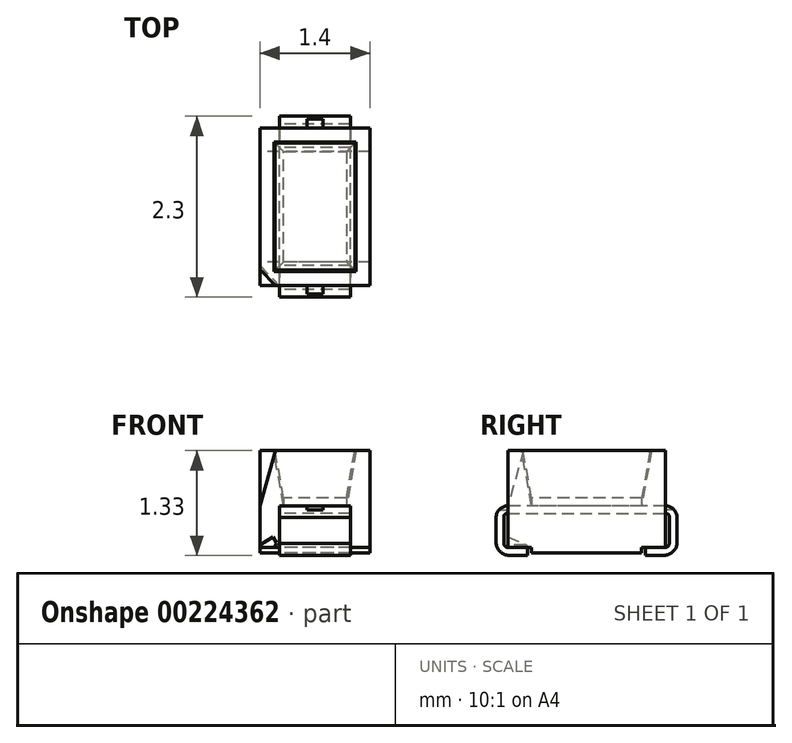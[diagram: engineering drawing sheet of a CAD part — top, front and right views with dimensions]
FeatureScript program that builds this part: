
annotation { "Feature Type Name" : "Feature", "Feature Type Description" : "" }
export const myFeature = defineFeature(function(context is Context, id is Id, definition is map)
    precondition{}
    {
        {
            var Q0;
            Q0=qCreatedBy(makeId("Top.planeOp"),FACE);
            var sketch = newSketch(context, id + "F0", { "sketchPlane" : qUnion([Q0])});
            skLineSegment(sketch, "E0.bottom", {"start": v(0.7, -1) * mm, "end": v(-0.7, -1) * mm});
            skLineSegment(sketch, "E0.top", {"start": v(0.7, 1) * mm, "end": v(-0.7, 1) * mm});
            skLineSegment(sketch, "E0.left", {"start": v(0.7, -1) * mm, "end": v(0.7, 1) * mm});
            skLineSegment(sketch, "E0.right", {"start": v(-0.7, -1) * mm, "end": v(-0.7, 1) * mm});
            skPoint(sketch, "E0.middle", {"position": v(0, 0) * mm});
            skLineSegment(sketch, "E1.bottom", {"start": v(0.4, -0.7) * mm, "end": v(-0.4, -0.7) * mm});
            skLineSegment(sketch, "E1.top", {"start": v(0.4, 0.7) * mm, "end": v(-0.4, 0.7) * mm});
            skLineSegment(sketch, "E1.left", {"start": v(0.4, -0.7) * mm, "end": v(0.4, 0.7) * mm});
            skLineSegment(sketch, "E1.right", {"start": v(-0.4, -0.7) * mm, "end": v(-0.4, 0.7) * mm});
            skLineSegment(sketch, "E2.bottom", {"start": v(0.15, -0.4) * mm, "end": v(-0.15, -0.4) * mm});
            skLineSegment(sketch, "E2.top", {"start": v(0.15, -0.1) * mm, "end": v(-0.15, -0.1) * mm});
            skLineSegment(sketch, "E2.left", {"start": v(0.15, -0.4) * mm, "end": v(0.15, -0.1) * mm});
            skLineSegment(sketch, "E2.right", {"start": v(-0.15, -0.4) * mm, "end": v(-0.15, -0.1) * mm});
            skPoint(sketch, "E2.middle", {"position": v(0, -0.25) * mm});
            skSolve(sketch);
        }
        {
            var Q0;
            Q0=makeQuery(id+"F0.imprint","IMPRINT",FACE,{"disambiguationData":[TD([[makeQuery(id+"F0.imprint","IMPRINT",EDGE,{"derivedFrom":sQuery(id+"F0.wireOp",EDGE,"E0.bottom")}),-1.0]])]});
            var Q1;
            {var subQ1=sQuery(id+"F0.wireOp",EDGE,"E0.top");Q1=makeQuery(id+"F0.imprint","IMPRINT",FACE,{"disambiguationData":[TD([[makeQuery(id+"F0.imprint","IMPRINT",EDGE,{"derivedFrom":subQ1}),1.0]])]});}
            extrude(context, id + "F1", {"entities" : qUnion([Q0, Q1]), "depth" : .7 * mm, "hasSecondDirection" : true, "secondDirectionOppositeDirection" : true, "secondDirectionDepth" : .6 * mm});
        }
        {
            var Q0;
            Q0=makeQuery(id+"F0.imprint","IMPRINT",FACE,{"disambiguationData":[TD([[makeQuery(id+"F0.imprint","IMPRINT",EDGE,{"derivedFrom":sQuery(id+"F0.wireOp",EDGE,"E1.bottom")}),-1.0]])]});
            var Q1;
            Q1=makeQuery(id+"F1.opExtrude","CAP_FACE",FACE,{"disambiguationData":[OSD([sQuery(id+"F0.wireOp",EDGE,"E0.bottom"),sQuery(id+"F0.wireOp",EDGE,"E0.top"),sQuery(id+"F0.wireOp",EDGE,"E0.left"),sQuery(id+"F0.wireOp",EDGE,"E0.right"),sQuery(id+"F0.wireOp",EDGE,"E1.bottom"),sQuery(id+"F0.wireOp",EDGE,"E1.top"),sQuery(id+"F0.wireOp",EDGE,"E1.left"),sQuery(id+"F0.wireOp",EDGE,"E1.right")])],"isStart":false});
            extrude(context, id + "F2", {"entities" : qUnion([Q0]), "operationType" : NewBodyOperationType.REMOVE, "endBound" : BoundingType.UP_TO_SURFACE, "endBoundEntityFace" : qUnion([Q1]), "depth" : 25 * mm, "hasDraft" : true, "draftAngle" : 10 * degree});
        }
        {
            var Q0;
            Q0=makeQuery(id+"F0.imprint","IMPRINT",FACE,{"disambiguationData":[TD([[makeQuery(id+"F0.imprint","IMPRINT",EDGE,{"derivedFrom":sQuery(id+"F0.wireOp",EDGE,"E2.bottom")}),-1.0]])]});
            extrude(context, id + "F3", {"entities" : qUnion([Q0]), "depth" : .1 * mm});
        }
        {
            var Q0;
            Q0=makeQuery(id+"F0.imprint","IMPRINT",FACE,{"disambiguationData":[TD([[makeQuery(id+"F0.imprint","IMPRINT",EDGE,{"derivedFrom":sQuery(id+"F0.wireOp",EDGE,"E1.bottom")}),-1.0]])]});
            var Q1;
            Q1=makeQuery(id+"F1.opExtrude","CAP_FACE",FACE,{"disambiguationData":[OSD([sQuery(id+"F0.wireOp",EDGE,"E0.bottom"),sQuery(id+"F0.wireOp",EDGE,"E0.top"),sQuery(id+"F0.wireOp",EDGE,"E0.left"),sQuery(id+"F0.wireOp",EDGE,"E0.right"),sQuery(id+"F0.wireOp",EDGE,"E1.bottom"),sQuery(id+"F0.wireOp",EDGE,"E1.top"),sQuery(id+"F0.wireOp",EDGE,"E1.left"),sQuery(id+"F0.wireOp",EDGE,"E1.right")])],"isStart":true});
            extrude(context, id + "F4", {"entities" : qUnion([Q0]), "operationType" : NewBodyOperationType.ADD, "endBound" : BoundingType.UP_TO_SURFACE, "oppositeDirection" : true, "endBoundEntityFace" : qUnion([Q1]), "depth" : 25 * mm});
        }
        {
            var Q0;
            Q0=makeQuery(id+"F0.imprint","IMPRINT",FACE,{"disambiguationData":[TD([[makeQuery(id+"F0.imprint","IMPRINT",EDGE,{"derivedFrom":sQuery(id+"F0.wireOp",EDGE,"E1.bottom")}),-1.0]])]});
            extrude(context, id + "F5", {"entities" : qUnion([Q0]), "depth" : .1 * mm});
        }
        {
            var Q0;
            Q0=makeQuery(id+"F0.imprint","IMPRINT",FACE,{"disambiguationData":[TD([[makeQuery(id+"F0.imprint","IMPRINT",EDGE,{"derivedFrom":sQuery(id+"F0.wireOp",EDGE,"E2.bottom")}),-1.0]])]});
            var Q1;
            {var subQ0=sQuery(id+"F0.wireOp",EDGE,"E1.right");var subQ1=sQuery(id+"F0.wireOp",EDGE,"E1.left");var subQ2=sQuery(id+"F0.wireOp",EDGE,"E1.top");var subQ3=sQuery(id+"F0.wireOp",EDGE,"E1.bottom");var subQ4=sQuery(id+"F0.wireOp",EDGE,"E0.right");var subQ5=sQuery(id+"F0.wireOp",EDGE,"E0.left");var subQ6=sQuery(id+"F0.wireOp",EDGE,"E0.top");var subQ7=sQuery(id+"F0.wireOp",EDGE,"E0.bottom");Q1=makeQuery(id+"F4.boolean.opBoolean","MERGE",FACE,{"derivedFrom":[makeQuery(id+"F1.opExtrude","CAP_FACE",FACE,{"disambiguationData":[OSD([subQ7,subQ6,subQ5,subQ4,subQ3,subQ2,subQ1,subQ0])],"isStart":true}),makeQuery(id+"F4.opExtrude","CAP_FACE",FACE,{"disambiguationData":[OSD([subQ7,subQ6,subQ5,subQ4,subQ3,subQ2,subQ1,subQ0])],"isStart":false})]});}
            extrude(context, id + "F6", {"entities" : qUnion([Q0]), "operationType" : NewBodyOperationType.ADD, "endBound" : BoundingType.UP_TO_SURFACE, "oppositeDirection" : true, "endBoundEntityFace" : qUnion([Q1]), "depth" : 25 * mm});
        }
        {
            var Q0;
            Q0=makeQuery(id+"F1.opExtrude","SWEPT_FACE",FACE,{"disambiguationData":[OSD([sQuery(id+"F0.wireOp",EDGE,"E0.right")])]});
            var sketch = newSketch(context, id + "F7", { "sketchPlane" : qUnion([Q0])});
            skLineSegment(sketch, "E3", {"start": v(-1, 0.7) * mm, "end": v(1, 0.7) * mm, "construction": true});
            skLineSegment(sketch, "E4", {"start": v(1, 0.7) * mm, "end": v(1, -0.6) * mm, "construction": true});
            skLineSegment(sketch, "E5", {"start": v(1, -0.6) * mm, "end": v(-1, -0.6) * mm, "construction": true});
            skLineSegment(sketch, "E6", {"start": v(-1, -0.6) * mm, "end": v(-1, 0.7) * mm, "construction": true});
            skLineSegment(sketch, "E7", {"start": v(-1.16, -0.53) * mm, "end": v(-0.7, -0.53) * mm});
            skLineSegment(sketch, "E8", {"start": v(-0.7, -0.53) * mm, "end": v(-0.7, -0.74) * mm});
            skLineSegment(sketch, "E9", {"start": v(-0.7, -0.74) * mm, "end": v(0.7, -0.74) * mm});
            skLineSegment(sketch, "E10", {"start": v(0.7, -0.74) * mm, "end": v(0.7, -0.53) * mm});
            skLineSegment(sketch, "E11", {"start": v(0.7, -0.53) * mm, "end": v(1.16, -0.53) * mm});
            skLineSegment(sketch, "E12", {"start": v(1.16, -0.53) * mm, "end": v(1.16, -0.97) * mm});
            skLineSegment(sketch, "E13", {"start": v(1.16, -0.97) * mm, "end": v(-1.16, -0.97) * mm});
            skLineSegment(sketch, "E14", {"start": v(-1.16, -0.97) * mm, "end": v(-1.16, -0.53) * mm});
            skSolve(sketch);
        }
        {
            var Q0;
            {var subQ0=sQuery(id+"F7.wireOp",EDGE,"E8");var subQ1=sQuery(id+"F7.wireOp",EDGE,"E7");var subQ2=makeQuery(id+"F7.imprint","INTERSECT",VERTEX,{"derivedFrom":[subQ1,subQ0]});Q0=makeQuery(id+"F7.imprint","IMPRINT",FACE,{"disambiguationData":[TD([[makeQuery(id+"F7.imprint","IMPRINT",EDGE,{"disambiguationData":[TD([[subQ2,-1.0]])],"derivedFrom":subQ0}),-1.0]])]});}
            var Q1;
            {var subQ0=sQuery(id+"F7.wireOp",EDGE,"E11");var subQ1=sQuery(id+"F7.wireOp",EDGE,"E10");var subQ2=makeQuery(id+"F7.imprint","INTERSECT",VERTEX,{"derivedFrom":[subQ1,subQ0]});Q1=makeQuery(id+"F7.imprint","IMPRINT",FACE,{"disambiguationData":[TD([[makeQuery(id+"F7.imprint","IMPRINT",EDGE,{"disambiguationData":[TD([[subQ2,1.0]])],"derivedFrom":subQ1}),-1.0]])]});}
            extrude(context, id + "F8", {"entities" : qUnion([Q0, Q1]), "operationType" : NewBodyOperationType.REMOVE, "endBound" : BoundingType.UP_TO_NEXT, "oppositeDirection" : true, "depth" : 25 * mm});
        }
        {
            var Q0;
            Q0=makeQuery(id+"F1.opExtrude","SWEPT_FACE",FACE,{"disambiguationData":[OSD([sQuery(id+"F0.wireOp",EDGE,"E0.right")])]});
            var sketch = newSketch(context, id + "F9", { "sketchPlane" : qUnion([Q0])});
            skLineSegment(sketch, "E15", {"start": v(-1, 0) * mm, "end": v(1, 0) * mm, "construction": true});
            skLineSegment(sketch, "E16", {"start": v(-1.15, -0.15) * mm, "end": v(-1.15, -0.48) * mm});
            skLineSegment(sketch, "E17", {"start": v(-1, -0.63) * mm, "end": v(-0.75, -0.63) * mm});
            skLineSegment(sketch, "E18", {"start": v(-1.15, 0) * mm, "end": v(1.15, 0) * mm});
            skLineSegment(sketch, "E19", {"start": v(1.15, -0.15) * mm, "end": v(1.15, -0.48) * mm});
            skLineSegment(sketch, "E20", {"start": v(1, -0.63) * mm, "end": v(0.75, -0.63) * mm});
            skLineSegment(sketch, "E21", {"start": v(0.75, -0.63) * mm, "end": v(0.75, -0.53) * mm});
            skLineSegment(sketch, "E22", {"start": v(0.75, -0.53) * mm, "end": v(1, -0.53) * mm});
            skLineSegment(sketch, "E23", {"start": v(1.05, -0.48) * mm, "end": v(1.05, -0.15) * mm});
            skLineSegment(sketch, "E24", {"start": v(1, -0.1) * mm, "end": v(-1, -0.1) * mm});
            skLineSegment(sketch, "E25", {"start": v(-1.05, -0.15) * mm, "end": v(-1.05, -0.48) * mm});
            skLineSegment(sketch, "E26", {"start": v(-1, -0.53) * mm, "end": v(-0.75, -0.53) * mm});
            skLineSegment(sketch, "E27", {"start": v(-0.75, -0.53) * mm, "end": v(-0.75, -0.63) * mm});
            skPoint(sketch, "E28.visualSharp", {"position": v(-1.05, -0.1) * mm});
            skArc(sketch, "E28.filletArc", {"start": v(-1, -0.1) * mm, "mid": v(-1.04, -0.11) * mm, "end": v(-1.05, -0.15) * mm});
            skPoint(sketch, "E29.newPointA", {"position": v(0, 0) * mm});
            skArc(sketch, "E29.filletArc", {"start": v(-1, 0) * mm, "mid": v(-1.1, -0.04) * mm, "end": v(-1.15, -0.15) * mm});
            skPoint(sketch, "E30.visualSharp", {"position": v(-1.15, -0.63) * mm});
            skArc(sketch, "E30.filletArc", {"start": v(-1.15, -0.48) * mm, "mid": v(-1.1, -0.58) * mm, "end": v(-1, -0.63) * mm});
            skPoint(sketch, "E31.visualSharp", {"position": v(-1.05, -0.53) * mm});
            skArc(sketch, "E31.filletArc", {"start": v(-1.05, -0.48) * mm, "mid": v(-1.04, -0.51) * mm, "end": v(-1, -0.53) * mm});
            skPoint(sketch, "E32.visualSharp", {"position": v(1.05, -0.53) * mm});
            skArc(sketch, "E32.filletArc", {"start": v(1, -0.53) * mm, "mid": v(1.04, -0.51) * mm, "end": v(1.05, -0.48) * mm});
            skPoint(sketch, "E33.visualSharp", {"position": v(1.05, -0.1) * mm});
            skArc(sketch, "E33.filletArc", {"start": v(1.05, -0.15) * mm, "mid": v(1.04, -0.11) * mm, "end": v(1, -0.1) * mm});
            skArc(sketch, "E34.filletArc", {"start": v(1.15, -0.15) * mm, "mid": v(1.1, -0.04) * mm, "end": v(1, 0) * mm});
            skPoint(sketch, "E35.visualSharp", {"position": v(1.15, -0.63) * mm});
            skArc(sketch, "E35.filletArc", {"start": v(1, -0.63) * mm, "mid": v(1.1, -0.58) * mm, "end": v(1.15, -0.48) * mm});
            skSolve(sketch);
        }
        {
            var Q0;
            Q0=qSketchRegion(id+"F9",true);
            var Q1;
            Q1=makeQuery(id+"F1.opExtrude","SWEPT_FACE",FACE,{"disambiguationData":[OSD([sQuery(id+"F0.wireOp",EDGE,"E0.left")])]});
            extrude(context, id + "F10", {"entities" : qUnion([Q0]), "oppositeDirection" : true, "endBoundEntityFace" : qUnion([Q1]), "depth" : 1.15 * mm, "hasSecondDirection" : true, "secondDirectionOppositeDirection" : true, "secondDirectionDepth" : .25 * mm});
        }
        {
            var Q0;
            Q0=makeQuery(id+"F5.opExtrude","CAP_FACE",FACE,{"disambiguationData":[OSD([sQuery(id+"F0.wireOp",EDGE,"E1.bottom"),sQuery(id+"F0.wireOp",EDGE,"E1.top"),sQuery(id+"F0.wireOp",EDGE,"E1.left"),sQuery(id+"F0.wireOp",EDGE,"E1.right"),sQuery(id+"F0.wireOp",EDGE,"E2.bottom"),sQuery(id+"F0.wireOp",EDGE,"E2.top"),sQuery(id+"F0.wireOp",EDGE,"E2.left"),sQuery(id+"F0.wireOp",EDGE,"E2.right")])],"isStart":false});
            var sketch = newSketch(context, id + "F11", { "sketchPlane" : qUnion([Q0])});
            skLineSegment(sketch, "E36.0.1", {"start": v(-0.45, 1) * mm, "end": v(0.45, 1) * mm});
            skLineSegment(sketch, "E37", {"start": v(0, 1) * mm, "end": v(0.1, 1) * mm});
            skLineSegment(sketch, "E38", {"start": v(0.1, 1) * mm, "end": v(0.1, 1.2) * mm});
            skLineSegment(sketch, "E39", {"start": v(0.1, 1.2) * mm, "end": v(-0.1, 1.2) * mm});
            skLineSegment(sketch, "E40", {"start": v(-0.1, 1.2) * mm, "end": v(-0.1, 1) * mm});
            skLineSegment(sketch, "E41", {"start": v(-0.1, 1) * mm, "end": v(0, 1) * mm});
            skPoint(sketch, "E42.startSnap0", {"position": v(-0.15, -0.25) * mm});
            skPoint(sketch, "E36.0.2.end.orphan", {"position": v(0.45, 1.15) * mm});
            skPoint(sketch, "E36.0.0.start.orphan", {"position": v(-0.45, 1.15) * mm});
            skLineSegment(sketch, "E43", {"start": v(-0.78, 0) * mm, "end": v(1.2, 0) * mm, "construction": true});
            skLineSegment(sketch, "E44.MirrorCS", {"start": v(-0.1, -1) * mm, "end": v(0, -1) * mm});
            skLineSegment(sketch, "E45.MirrorCS", {"start": v(-0.1, -1.2) * mm, "end": v(-0.1, -1) * mm});
            skLineSegment(sketch, "E46.MirrorCS", {"start": v(0, -1) * mm, "end": v(0.1, -1) * mm});
            skLineSegment(sketch, "E47.MirrorCS", {"start": v(0.1, -1.2) * mm, "end": v(-0.1, -1.2) * mm});
            skLineSegment(sketch, "E48.MirrorCS", {"start": v(0.1, -1) * mm, "end": v(0.1, -1.2) * mm});
            skSolve(sketch);
        }
        {
            var Q0;
            Q0=qSketchRegion(id+"F11",true);
            extrude(context, id + "F12", {"entities" : qUnion([Q0]), "operationType" : NewBodyOperationType.REMOVE, "oppositeDirection" : true, "depth" : .15 * mm});
        }
        {
            var Q0;
            Q0=makeQuery(id+"F1.opExtrude","SWEPT_FACE",FACE,{"disambiguationData":[OSD([sQuery(id+"F0.wireOp",EDGE,"E0.bottom")])]});
            var sketch = newSketch(context, id + "F13", { "sketchPlane" : qUnion([Q0])});
            skLineSegment(sketch, "E49", {"start": v(-0.7, 0) * mm, "end": v(-0.5, 0.7) * mm});
            skLineSegment(sketch, "E50", {"start": v(-0.7, -0.13) * mm, "end": v(-0.45, -0.53) * mm});
            skSolve(sketch);
        }
        {
            var Q0;
            Q0=makeQuery(id+"F1.opExtrude","SWEPT_FACE",FACE,{"disambiguationData":[OSD([sQuery(id+"F0.wireOp",EDGE,"E0.right")])]});
            var sketch = newSketch(context, id + "F14", { "sketchPlane" : qUnion([Q0])});
            skLineSegment(sketch, "E51", {"start": v(0.8, 0.7) * mm, "end": v(1, 0) * mm});
            skLineSegment(sketch, "E52", {"start": v(1, 0) * mm, "end": v(1, 0.7) * mm});
            skLineSegment(sketch, "E53", {"start": v(0.7, -0.53) * mm, "end": v(1, -0.53) * mm});
            skLineSegment(sketch, "E54", {"start": v(1, 0.7) * mm, "end": v(1, -0.53) * mm});
            skLineSegment(sketch, "E55", {"start": v(1, 0.7) * mm, "end": v(-1, 0.7) * mm});
            skLineSegment(sketch, "E56", {"start": v(-1, 0.7) * mm, "end": v(-1, -0.53) * mm});
            skLineSegment(sketch, "E57", {"start": v(-1, -0.53) * mm, "end": v(-0.7, -0.53) * mm});
            skLineSegment(sketch, "E58", {"start": v(-0.7, -0.53) * mm, "end": v(-0.7, -0.6) * mm});
            skLineSegment(sketch, "E59", {"start": v(0.7, -0.6) * mm, "end": v(-0.7, -0.6) * mm});
            skLineSegment(sketch, "E60", {"start": v(0.7, -0.6) * mm, "end": v(0.7, -0.53) * mm});
            skLineSegment(sketch, "E61", {"start": v(1, -0.13) * mm, "end": v(0.75, -0.53) * mm});
            skSolve(sketch);
        }
        {
            var Q0;
            Q0=makeQuery(id+"F1.opExtrude","CAP_FACE",FACE,{"disambiguationData":[OSD([sQuery(id+"F0.wireOp",EDGE,"E0.bottom"),sQuery(id+"F0.wireOp",EDGE,"E0.top"),sQuery(id+"F0.wireOp",EDGE,"E0.left"),sQuery(id+"F0.wireOp",EDGE,"E0.right"),sQuery(id+"F0.wireOp",EDGE,"E1.bottom"),sQuery(id+"F0.wireOp",EDGE,"E1.top"),sQuery(id+"F0.wireOp",EDGE,"E1.left"),sQuery(id+"F0.wireOp",EDGE,"E1.right")])],"isStart":false});
            var sketch = newSketch(context, id + "F15", { "sketchPlane" : qUnion([Q0])});
            skLineSegment(sketch, "E62", {"start": v(-0.7, -0.8) * mm, "end": v(-0.5, -1) * mm});
            skSolve(sketch);
        }
        {
            var Q0;
            Q0=sQuery(id+"F15.wireOp",VERTEX,"E62.start");
            var Q1;
            Q1=sQuery(id+"F15.wireOp",VERTEX,"E62.end");
            var Q2;
            Q2=sQuery(id+"F14.wireOp",VERTEX,"E52.start");
            cPlane(context, id + "F16", {"entities" : qUnion([Q0, Q1, Q2]), "cplaneType" : CPlaneType.THREE_POINT, "offset" : 25 * mm, "width" : 150 * mm, "height" : 150 * mm});
        }
        {
            var Q0;
            Q0=qCreatedBy(id+"F16.planeOp",FACE);
            var sketch = newSketch(context, id + "F17", { "sketchPlane" : qUnion([Q0])});
            skLineSegment(sketch, "E63.bottom", {"start": v(-0.04, 0.54) * mm, "end": v(0.57, 0.54) * mm});
            skLineSegment(sketch, "E63.top", {"start": v(-0.04, -0.39) * mm, "end": v(0.57, -0.39) * mm});
            skLineSegment(sketch, "E63.left", {"start": v(-0.04, 0.54) * mm, "end": v(-0.04, -0.39) * mm});
            skLineSegment(sketch, "E63.right", {"start": v(0.57, 0.54) * mm, "end": v(0.57, -0.39) * mm});
            skSolve(sketch);
        }
        {
            var Q0;
            Q0=qSketchRegion(id+"F17",true);
            extrude(context, id + "F18", {"entities" : qUnion([Q0]), "operationType" : NewBodyOperationType.REMOVE, "endBound" : BoundingType.UP_TO_NEXT, "depth" : 25 * mm});
        }
        {
            var Q0;
            Q0=makeQuery(id+"F8.boolean.opBoolean","COPY",FACE,{"derivedFrom":makeQuery(id+"F8.opExtrude","SWEPT_FACE",FACE,{"disambiguationData":[OSD([sQuery(id+"F7.wireOp",EDGE,"E11")])]})});
            var sketch = newSketch(context, id + "F19", { "sketchPlane" : qUnion([Q0])});
            skLineSegment(sketch, "E64", {"start": v(-0.7, 0.75) * mm, "end": v(-0.45, 1) * mm});
            skSolve(sketch);
        }
        {
            var Q0;
            Q0=sQuery(id+"F19.wireOp",VERTEX,"E64.start");
            var Q1;
            Q1=sQuery(id+"F19.wireOp",VERTEX,"E64.end");
            var Q2;
            Q2=sQuery(id+"F14.wireOp",VERTEX,"E61.start");
            cPlane(context, id + "F20", {"entities" : qUnion([Q0, Q1, Q2]), "cplaneType" : CPlaneType.THREE_POINT, "offset" : 25 * mm, "width" : 150 * mm, "height" : 150 * mm});
        }
        {
            var Q0;
            Q0=qCreatedBy(id+"F20.planeOp",FACE);
            var sketch = newSketch(context, id + "F21", { "sketchPlane" : qUnion([Q0])});
            skLineSegment(sketch, "E65.0", {"start": v(-0.34, 0.26) * mm, "end": v(0, -0.07) * mm});
            skLineSegment(sketch, "E65.1", {"start": v(-0.34, 0.26) * mm, "end": v(-0.34, -0.2) * mm});
            skLineSegment(sketch, "E65.2", {"start": v(0, -0.07) * mm, "end": v(-0.34, -0.2) * mm});
            skSolve(sketch);
        }
        {
            var Q0;
            Q0=qSketchRegion(id+"F21",true);
            extrude(context, id + "F22", {"entities" : qUnion([Q0]), "operationType" : NewBodyOperationType.REMOVE, "endBound" : BoundingType.THROUGH_ALL, "oppositeDirection" : true, "depth" : 25 * mm});
        }
        {
            var Q0;
            Q0=makeQuery(id+"F5.opExtrude","CAP_FACE",FACE,{"disambiguationData":[OSD([sQuery(id+"F0.wireOp",EDGE,"E1.bottom"),sQuery(id+"F0.wireOp",EDGE,"E1.top"),sQuery(id+"F0.wireOp",EDGE,"E1.left"),sQuery(id+"F0.wireOp",EDGE,"E1.right"),sQuery(id+"F0.wireOp",EDGE,"E2.bottom"),sQuery(id+"F0.wireOp",EDGE,"E2.top"),sQuery(id+"F0.wireOp",EDGE,"E2.left"),sQuery(id+"F0.wireOp",EDGE,"E2.right")])],"isStart":false});
            var sketch = newSketch(context, id + "F23", { "sketchPlane" : qUnion([Q0])});
            skLineSegment(sketch, "E66", {"start": v(-0.4, 0.7) * mm, "end": v(0.4, 0.7) * mm});
            skLineSegment(sketch, "E67", {"start": v(0.4, 0.7) * mm, "end": v(0.4, -0.7) * mm});
            skLineSegment(sketch, "E68", {"start": v(0.4, -0.7) * mm, "end": v(-0.4, -0.7) * mm});
            skLineSegment(sketch, "E69", {"start": v(-0.4, -0.7) * mm, "end": v(-0.4, 0.7) * mm});
            skSolve(sketch);
        }
        {
            var Q0;
            Q0 = qSketchRegion(id + "F23", true);
            var Q1;
            Q1=makeQuery(id+"F1.opExtrude","CAP_FACE",FACE,{"disambiguationData":[OSD([sQuery(id+"F0.wireOp",EDGE,"E0.bottom"),sQuery(id+"F0.wireOp",EDGE,"E0.top"),sQuery(id+"F0.wireOp",EDGE,"E0.left"),sQuery(id+"F0.wireOp",EDGE,"E0.right"),sQuery(id+"F0.wireOp",EDGE,"E1.bottom"),sQuery(id+"F0.wireOp",EDGE,"E1.top"),sQuery(id+"F0.wireOp",EDGE,"E1.left"),sQuery(id+"F0.wireOp",EDGE,"E1.right")])],"isStart":false});
            extrude(context, id + "F24", {"entities" : qUnion([Q0]), "endBound" : BoundingType.UP_TO_SURFACE, "endBoundEntityFace" : qUnion([Q1]), "depth" : 25 * mm, "hasDraft" : true, "draftAngle" : 10 * degree});
        }
    });
